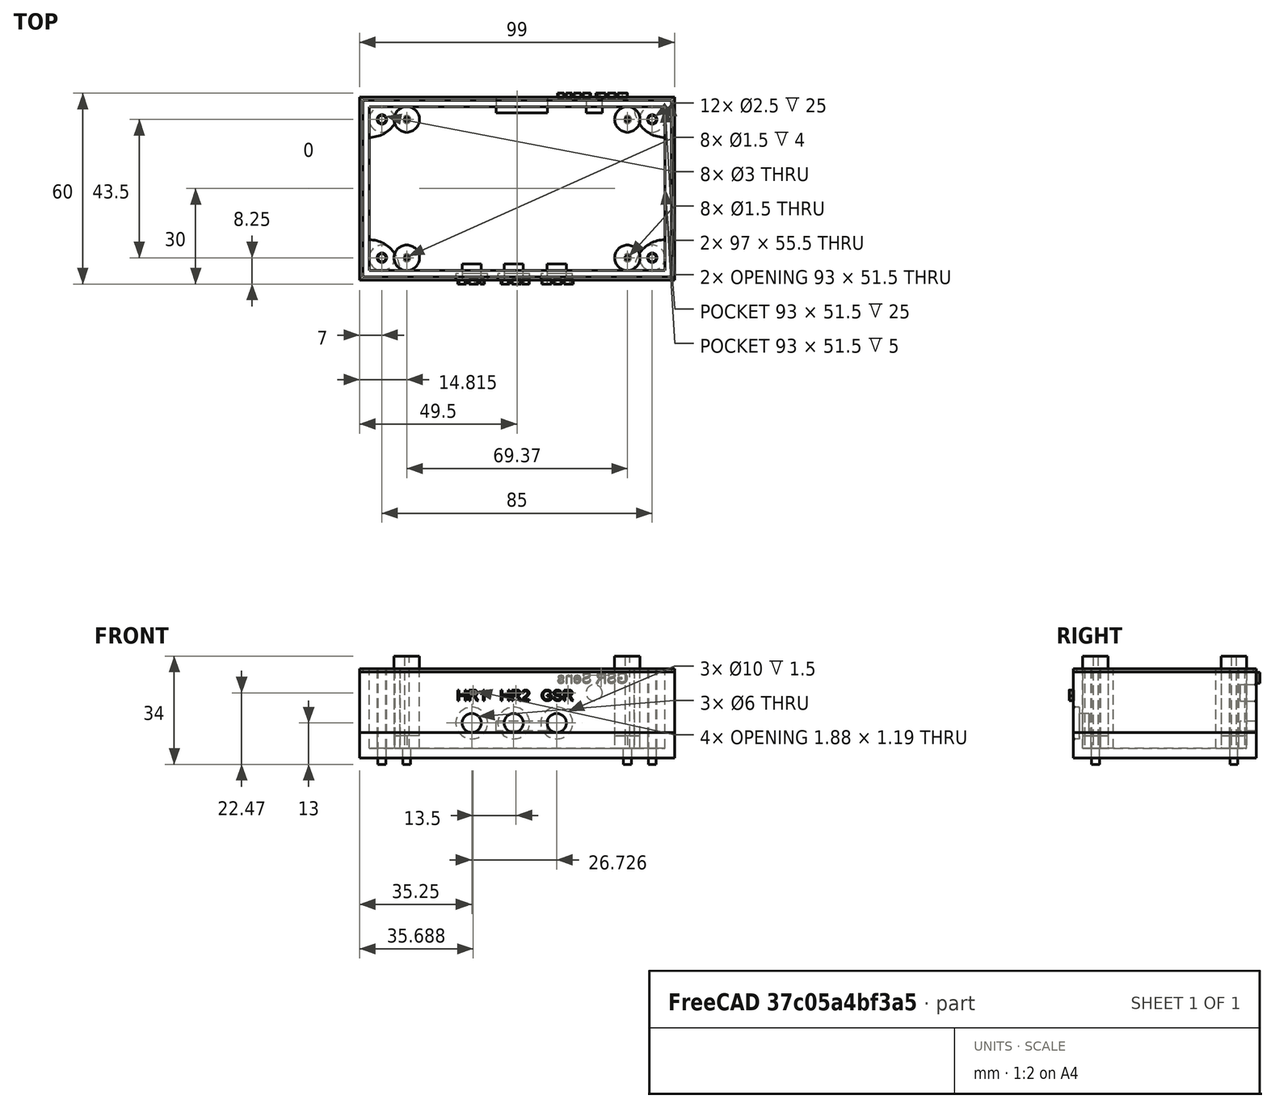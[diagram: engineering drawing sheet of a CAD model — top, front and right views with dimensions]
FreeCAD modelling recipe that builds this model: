
FCSTD DOCUMENT  (FreeCAD 0.15R4572 (Git))
Label: bottom2
License: All rights reserved
LicenseURL: http://en.wikipedia.org/wiki/All_rights_reserved
objects: Sketcher::SketchObject×22, PartDesign::Pad×13, PartDesign::Pocket×9, Part::Part2DObjectPython×4, PartDesign::Fillet×4, Part::Thickness×3, Part::Mirroring×1
note: 78 computed .brp shape members not serialized (recipe doc carries the construction recipe); baked Part::Feature solids carry a one-line shape summary decoded from their .brp

FEATURE [Sketcher::SketchObject] Sketch  label="Под отверстия платы"
  sketch-geometry (12):
    g0: LineSegment [constr] StartX=-34.685 StartY=21.75 StartZ=0 EndX=34.685 EndY=21.75 EndZ=0
    g1: LineSegment [constr] StartX=34.685 StartY=21.75 StartZ=0 EndX=34.685 EndY=-21.75 EndZ=0
    g2: LineSegment [constr] StartX=34.685 StartY=-21.75 StartZ=0 EndX=-34.685 EndY=-21.75 EndZ=0
    g3: LineSegment [constr] StartX=-34.685 StartY=-21.75 StartZ=0 EndX=-34.685 EndY=21.75 EndZ=0
    g4: Circle CenterX=-34.685 CenterY=21.75 CenterZ=0 NormalX=0 NormalY=0 NormalZ=1 Radius=0.75
    g5: Circle CenterX=-34.685 CenterY=-21.75 CenterZ=0 NormalX=0 NormalY=0 NormalZ=1 Radius=0.75
    g6: Circle CenterX=34.685 CenterY=-21.75 CenterZ=0 NormalX=0 NormalY=0 NormalZ=1 Radius=0.75
    g7: Circle CenterX=34.685 CenterY=21.75 CenterZ=0 NormalX=0 NormalY=0 NormalZ=1 Radius=0.75
    g8: Circle CenterX=-34.685 CenterY=21.75 CenterZ=0 NormalX=0 NormalY=0 NormalZ=1 Radius=4
    g9: Circle CenterX=-34.685 CenterY=-21.75 CenterZ=0 NormalX=0 NormalY=0 NormalZ=1 Radius=4
    g10: Circle CenterX=34.685 CenterY=-21.75 CenterZ=0 NormalX=0 NormalY=0 NormalZ=1 Radius=4
    g11: Circle CenterX=34.685 CenterY=21.75 CenterZ=0 NormalX=0 NormalY=0 NormalZ=1 Radius=4
  constraints (28):
    c: Coincident(g0,g1)
    c: Coincident(g1,g2)
    c: Coincident(g2,g3)
    c: Coincident(g3,g0)
    c: Horizontal(g0)
    c: Horizontal(g2)
    c: Vertical(g1)
    c: Vertical(g3)
    c: Symmetric(g0,g0,g-2)
    c: Symmetric(g0,g2,g-1)
    c: DistanceX(g0) = 69.37
    c: DistanceY(g0,g1) = -43.5
    c: Coincident(g4,g0)
    c: Coincident(g5,g2)
    c: Coincident(g6,g1)
    c: Coincident(g7,g0)
    c: Equal(g4,g7)
    c: Equal(g6,g5)
    c: Equal(g5,g4)
    c: Radius(g4) = 0.75
    c: Coincident(g8,g0)
    c: Coincident(g9,g2)
    c: Coincident(g10,g1)
    c: Coincident(g11,g0)
    c: Equal(g11,g8)
    c: Equal(g8,g9)
    c: Equal(g9,g10)
    c: Radius(g11) = 4
FEATURE [Sketcher::SketchObject] Sketch001  label="Маска платы"
  sketch-geometry (4):
    g0: LineSegment StartX=-38.25 StartY=25.25 StartZ=0 EndX=38.25 EndY=25.25 EndZ=0
    g1: LineSegment StartX=38.25 StartY=25.25 StartZ=0 EndX=38.25 EndY=-25.25 EndZ=0
    g2: LineSegment StartX=38.25 StartY=-25.25 StartZ=0 EndX=-38.25 EndY=-25.25 EndZ=0
    g3: LineSegment StartX=-38.25 StartY=-25.25 StartZ=0 EndX=-38.25 EndY=25.25 EndZ=0
  constraints (12):
    c: Coincident(g0,g1)
    c: Coincident(g1,g2)
    c: Coincident(g2,g3)
    c: Coincident(g3,g0)
    c: Horizontal(g0)
    c: Horizontal(g2)
    c: Vertical(g1)
    c: Vertical(g3)
    c: Symmetric(g0,g0,g-2)
    c: Symmetric(g0,g1,g-1)
    c: DistanceX(g0) = 76.5
    c: DistanceY(g1) = -50.5
FEATURE [Sketcher::SketchObject] Sketch002  label="Маска нижней части"
  sketch-geometry (8):
    g0: LineSegment [constr] StartX=-45 StartY=25 StartZ=0 EndX=45 EndY=25 EndZ=0
    g1: LineSegment [constr] StartX=45 StartY=25 StartZ=0 EndX=45 EndY=-25 EndZ=0
    g2: LineSegment [constr] StartX=45 StartY=-25 StartZ=0 EndX=-45 EndY=-25 EndZ=0
    g3: LineSegment [constr] StartX=-45 StartY=-25 StartZ=0 EndX=-45 EndY=25 EndZ=0
    g4: LineSegment StartX=-46.5 StartY=25.75 StartZ=0 EndX=46.5 EndY=25.75 EndZ=0
    g5: LineSegment StartX=46.5 StartY=25.75 StartZ=0 EndX=46.5 EndY=-25.75 EndZ=0
    g6: LineSegment StartX=46.5 StartY=-25.75 StartZ=0 EndX=-46.5 EndY=-25.75 EndZ=0
    g7: LineSegment StartX=-46.5 StartY=-25.75 StartZ=0 EndX=-46.5 EndY=25.75 EndZ=0
  constraints (24):
    c: Coincident(g0,g1)
    c: Coincident(g1,g2)
    c: Coincident(g2,g3)
    c: Coincident(g3,g0)
    c: Horizontal(g0)
    c: Horizontal(g2)
    c: Vertical(g1)
    c: Vertical(g3)
    c: Symmetric(g0,g0,g-2)
    c: Symmetric(g0,g1,g-1)
    c: DistanceX(g0) = 90
    c: DistanceY(g1) = -50
    c: Coincident(g4,g5)
    c: Coincident(g5,g6)
    c: Coincident(g6,g7)
    c: Coincident(g7,g4)
    c: Horizontal(g4)
    c: Horizontal(g6)
    c: Vertical(g5)
    c: Vertical(g7)
    c: Symmetric(g4,g5,g-1)
    c: Symmetric(g4,g4,g-2)
    c: DistanceY(g7) = 51.5
    c: DistanceX(g6) = -93
FEATURE [Sketcher::SketchObject] Sketch003  label="Отверстия под части корпуса"
  sketch-geometry (12):
    g0: LineSegment [constr] StartX=-42.5 StartY=21.75 StartZ=0 EndX=42.5 EndY=21.75 EndZ=0
    g1: LineSegment [constr] StartX=42.5 StartY=21.75 StartZ=0 EndX=42.5 EndY=-21.75 EndZ=0
    g2: LineSegment [constr] StartX=42.5 StartY=-21.75 StartZ=0 EndX=-42.5 EndY=-21.75 EndZ=0
    g3: LineSegment [constr] StartX=-42.5 StartY=-21.75 StartZ=0 EndX=-42.5 EndY=21.75 EndZ=0
    g4: Circle CenterX=-42.5 CenterY=21.75 CenterZ=0 NormalX=0 NormalY=0 NormalZ=1 Radius=1.5
    g5: Circle CenterX=-42.5 CenterY=21.75 CenterZ=0 NormalX=0 NormalY=0 NormalZ=1 Radius=4
    g6: Circle CenterX=-42.5 CenterY=-21.75 CenterZ=0 NormalX=0 NormalY=0 NormalZ=1 Radius=1.5
    g7: Circle CenterX=42.5 CenterY=-21.75 CenterZ=0 NormalX=0 NormalY=0 NormalZ=1 Radius=1.5
    g8: Circle CenterX=42.5 CenterY=21.75 CenterZ=0 NormalX=0 NormalY=0 NormalZ=1 Radius=1.5
    g9: Circle CenterX=-42.5 CenterY=-21.75 CenterZ=0 NormalX=0 NormalY=0 NormalZ=1 Radius=4
    g10: Circle CenterX=42.5 CenterY=-21.75 CenterZ=0 NormalX=0 NormalY=0 NormalZ=1 Radius=4
    g11: Circle CenterX=42.5 CenterY=21.75 CenterZ=0 NormalX=0 NormalY=0 NormalZ=1 Radius=4
  constraints (28):
    c: Coincident(g0,g1)
    c: Coincident(g1,g2)
    c: Coincident(g2,g3)
    c: Coincident(g3,g0)
    c: Horizontal(g0)
    c: Horizontal(g2)
    c: Vertical(g1)
    c: Vertical(g3)
    c: Symmetric(g1,g0,g-1)
    c: Symmetric(g0,g0,g-2)
    c: DistanceY(g1) = -43.5
    c: DistanceX(g0) = 85
    c: Coincident(g4,g0)
    c: Coincident(g5,g0)
    c: Coincident(g6,g2)
    c: Coincident(g7,g1)
    c: Coincident(g8,g0)
    c: Equal(g8,g7)
    c: Equal(g7,g6)
    c: Equal(g6,g4)
    c: Radius(g7) = 1.5
    c: Coincident(g9,g2)
    c: Coincident(g10,g1)
    c: Coincident(g11,g0)
    c: Equal(g11,g10)
    c: Equal(g10,g9)
    c: Equal(g9,g5)
    c: Radius(g9) = 4
FEATURE [PartDesign::Pad] Pad
  Length = 5
  Length2 = 100
  Sketch = -> Sketch002
  Type = 0
FEATURE [Part::Thickness] Thickness  label="Нижняя часть корпуса"
  Faces = -> Pad [Face6]
  Intersection = false
  Join = 2
  Mode = 0
  SelfIntersection = false
  Value = 3
FEATURE [PartDesign::Pad] Pad001  label="Под отверстия платы001"
  Length = 4
  Length2 = 100
  Sketch = -> Sketch
  Type = 0
FEATURE [PartDesign::Pad] Pad002  label="Отверстия под части корпуса001"
  Length = 5
  Length2 = 100
  Sketch = -> Sketch003
  Type = 0
FEATURE [Sketcher::SketchObject] Sketch004  label="Отверстия"
  sketch-geometry (16):
    g0: LineSegment [constr] StartX=-34.685 StartY=21.75 StartZ=0 EndX=34.685 EndY=21.75 EndZ=0
    g1: LineSegment [constr] StartX=34.685 StartY=21.75 StartZ=0 EndX=34.685 EndY=-21.75 EndZ=0
    g2: LineSegment [constr] StartX=34.685 StartY=-21.75 StartZ=0 EndX=-34.685 EndY=-21.75 EndZ=0
    g3: LineSegment [constr] StartX=-34.685 StartY=-21.75 StartZ=0 EndX=-34.685 EndY=21.75 EndZ=0
    g4: LineSegment [constr] StartX=-42.5 StartY=21.75 StartZ=0 EndX=42.5 EndY=21.75 EndZ=0
    g5: LineSegment [constr] StartX=42.5 StartY=21.75 StartZ=0 EndX=42.5 EndY=-21.75 EndZ=0
    g6: LineSegment [constr] StartX=42.5 StartY=-21.75 StartZ=0 EndX=-42.5 EndY=-21.75 EndZ=0
    g7: LineSegment [constr] StartX=-42.5 StartY=-21.75 StartZ=0 EndX=-42.5 EndY=21.75 EndZ=0
    g8: Circle CenterX=-42.5 CenterY=21.75 CenterZ=0 NormalX=0 NormalY=0 NormalZ=1 Radius=1.25
    g9: Circle CenterX=-34.685 CenterY=21.75 CenterZ=0 NormalX=0 NormalY=0 NormalZ=1 Radius=1.25
    g10: Circle CenterX=-42.5 CenterY=-21.75 CenterZ=0 NormalX=0 NormalY=0 NormalZ=1 Radius=1.25
    g11: Circle CenterX=-34.685 CenterY=-21.75 CenterZ=0 NormalX=0 NormalY=0 NormalZ=1 Radius=1.25
    g12: Circle CenterX=34.685 CenterY=-21.75 CenterZ=0 NormalX=0 NormalY=0 NormalZ=1 Radius=1.25
    g13: Circle CenterX=42.5 CenterY=-21.75 CenterZ=0 NormalX=0 NormalY=0 NormalZ=1 Radius=1.25
    g14: Circle CenterX=34.685 CenterY=21.75 CenterZ=0 NormalX=0 NormalY=0 NormalZ=1 Radius=1.25
    g15: Circle CenterX=42.5 CenterY=21.75 CenterZ=0 NormalX=0 NormalY=0 NormalZ=1 Radius=1.25
  constraints (40):
    c: Coincident(g0,g1)
    c: Coincident(g1,g2)
    c: Coincident(g2,g3)
    c: Coincident(g3,g0)
    c: Horizontal(g0)
    c: Horizontal(g2)
    c: Vertical(g1)
    c: Vertical(g3)
    c: Symmetric(g0,g0,g-2)
    c: DistanceX(g0) = 69.37
    c: Symmetric(g0,g1,g-1)
    c: DistanceY(g1) = -43.5
    c: Coincident(g4,g5)
    c: Coincident(g5,g6)
    c: Coincident(g6,g7)
    c: Coincident(g7,g4)
    c: Horizontal(g4)
    c: Horizontal(g6)
    c: Vertical(g5)
    c: Vertical(g7)
    c: Symmetric(g5,g4,g-1)
    c: Symmetric(g4,g4,g-2)
    c: DistanceY(g5) = -43.5
    c: DistanceX(g6,g5) = 85
    c: Coincident(g8,g4)
    c: Coincident(g9,g0)
    c: Coincident(g10,g6)
    c: Coincident(g11,g2)
    c: Coincident(g12,g1)
    c: Coincident(g13,g5)
    c: Coincident(g14,g0)
    c: Coincident(g15,g4)
    c: Equal(g15,g14)
    c: Equal(g14,g13)
    c: Equal(g13,g12)
    c: Equal(g12,g10)
    c: Equal(g10,g11)
    c: Equal(g11,g8)
    c: Equal(g8,g9)
    c: Radius(g8) = 1.25
FEATURE [Sketcher::SketchObject] Sketch005  label="Отверстия001"
  Support = -> Thickness [Face5]
  sketch-geometry (16):
    g0: LineSegment [constr] StartX=-34.7 StartY=21.75 StartZ=0 EndX=34.7 EndY=21.75 EndZ=0
    g1: LineSegment [constr] StartX=34.7 StartY=21.75 StartZ=0 EndX=34.7 EndY=-21.75 EndZ=0
    g2: LineSegment [constr] StartX=34.7 StartY=-21.75 StartZ=0 EndX=-34.7 EndY=-21.75 EndZ=0
    g3: LineSegment [constr] StartX=-34.7 StartY=-21.75 StartZ=0 EndX=-34.7 EndY=21.75 EndZ=0
    g4: LineSegment [constr] StartX=-42.5 StartY=21.75 StartZ=0 EndX=42.5 EndY=21.75 EndZ=0
    g5: LineSegment [constr] StartX=42.5 StartY=21.75 StartZ=0 EndX=42.5 EndY=-21.75 EndZ=0
    g6: LineSegment [constr] StartX=42.5 StartY=-21.75 StartZ=0 EndX=-42.5 EndY=-21.75 EndZ=0
    g7: LineSegment [constr] StartX=-42.5 StartY=-21.75 StartZ=0 EndX=-42.5 EndY=21.75 EndZ=0
    g8: Circle CenterX=-42.5 CenterY=21.75 CenterZ=0 NormalX=0 NormalY=0 NormalZ=1 Radius=1.25
    g9: Circle CenterX=-34.7 CenterY=21.75 CenterZ=0 NormalX=0 NormalY=0 NormalZ=1 Radius=1.25
    g10: Circle CenterX=34.7 CenterY=21.75 CenterZ=0 NormalX=0 NormalY=0 NormalZ=1 Radius=1.25
    g11: Circle CenterX=42.5 CenterY=21.75 CenterZ=0 NormalX=0 NormalY=0 NormalZ=1 Radius=1.25
    g12: Circle CenterX=42.5 CenterY=-21.75 CenterZ=0 NormalX=0 NormalY=0 NormalZ=1 Radius=1.25
    g13: Circle CenterX=34.7 CenterY=-21.75 CenterZ=0 NormalX=0 NormalY=0 NormalZ=1 Radius=1.25
    g14: Circle CenterX=-42.5 CenterY=-21.75 CenterZ=0 NormalX=0 NormalY=0 NormalZ=1 Radius=1.25
    g15: Circle CenterX=-34.7 CenterY=-21.75 CenterZ=0 NormalX=0 NormalY=0 NormalZ=1 Radius=1.25
  constraints (40):
    c: Coincident(g0,g1)
    c: Coincident(g1,g2)
    c: Coincident(g2,g3)
    c: Coincident(g3,g0)
    c: Horizontal(g0)
    c: Horizontal(g2)
    c: Vertical(g1)
    c: Vertical(g3)
    c: Coincident(g4,g5)
    c: Coincident(g5,g6)
    c: Coincident(g6,g7)
    c: Coincident(g7,g4)
    c: Horizontal(g4)
    c: Horizontal(g6)
    c: Vertical(g5)
    c: Vertical(g7)
    c: Symmetric(g5,g4,g-1)
    c: Symmetric(g4,g4,g-2)
    c: Symmetric(g0,g0,g-2)
    c: Symmetric(g0,g1,g-1)
    c: DistanceX(g0) = 69.4
    c: DistanceX(g6) = -85
    c: Equal(g5,g1)
    c: DistanceY(g7) = 43.5
    c: Coincident(g8,g4)
    c: Coincident(g9,g0)
    c: Equal(g8,g9)
    c: Radius(g8) = 1.25
    c: Coincident(g10,g0)
    c: Coincident(g11,g4)
    c: Coincident(g12,g5)
    c: Coincident(g13,g1)
    c: Coincident(g14,g6)
    c: Coincident(g15,g2)
    c: Equal(g14,g15)
    c: Equal(g15,g13)
    c: Equal(g13,g12)
    c: Equal(g12,g10)
    c: Equal(g10,g11)
    c: Equal(g9,g11)
FEATURE [PartDesign::Pocket] Pocket
  Length = 5
  Sketch = -> Sketch005
  Type = 0
FEATURE [Sketcher::SketchObject] Sketch006  label="Гайки"
  Placement = pos=(0,0,-3) rot=(1,0,0;3.14159rad)
  Support = -> Pocket [Face19]
  sketch-geometry (63):
    g0: LineSegment [constr] StartX=42.2536 StartY=21.75 StartZ=0 EndX=42.2536 EndY=-21.75 EndZ=0
    g1: LineSegment [constr] StartX=-42.2536 StartY=-21.75 StartZ=0 EndX=-42.2536 EndY=21.75 EndZ=0
    g2: Circle CenterX=-42.5 CenterY=-21.75 CenterZ=0 NormalX=0 NormalY=0 NormalZ=1 Radius=1.5
    g3: LineSegment StartX=-40.75 StartY=-24.7811 StartZ=0 EndX=-39 EndY=-21.75 EndZ=0
    g4: LineSegment StartX=-39 StartY=-21.75 StartZ=0 EndX=-40.75 EndY=-18.7189 EndZ=0
    g5: LineSegment StartX=-40.75 StartY=-18.7189 StartZ=0 EndX=-44.25 EndY=-18.7189 EndZ=0
    g6: LineSegment StartX=-44.25 StartY=-18.7189 StartZ=0 EndX=-46 EndY=-21.75 EndZ=0
    g7: LineSegment StartX=-46 StartY=-21.75 StartZ=0 EndX=-44.25 EndY=-24.7811 EndZ=0
    g8: LineSegment StartX=-44.25 StartY=-24.7811 StartZ=0 EndX=-40.75 EndY=-24.7811 EndZ=0
    g9: Circle [constr] CenterX=-42.5 CenterY=-21.75 CenterZ=0 NormalX=0 NormalY=0 NormalZ=1 Radius=3.5
    g10: LineSegment [constr] StartX=-34.7 StartY=-21.7429 StartZ=0 EndX=34.7 EndY=-21.7429 EndZ=0
    g11: LineSegment [constr] StartX=34.7 StartY=-21.7429 StartZ=0 EndX=34.7 EndY=21.7429 EndZ=0
    g12: LineSegment [constr] StartX=34.7 StartY=21.7429 StartZ=0 EndX=-34.7 EndY=21.7429 EndZ=0
    g13: LineSegment [constr] StartX=-34.7 StartY=21.7429 StartZ=0 EndX=-34.7 EndY=-21.7429 EndZ=0
    g14: LineSegment StartX=-32.95 StartY=-24.774 StartZ=0 EndX=-31.2 EndY=-21.7429 EndZ=0
    g15: LineSegment StartX=-31.2 StartY=-21.7429 StartZ=0 EndX=-32.95 EndY=-18.7118 EndZ=0
    g16: LineSegment StartX=-32.95 StartY=-18.7118 StartZ=0 EndX=-36.45 EndY=-18.7118 EndZ=0
    g17: LineSegment StartX=-36.45 StartY=-18.7118 StartZ=0 EndX=-38.2 EndY=-21.7429 EndZ=0
    g18: LineSegment StartX=-38.2 StartY=-21.7429 StartZ=0 EndX=-36.45 EndY=-24.774 EndZ=0
    g19: LineSegment StartX=-36.45 StartY=-24.774 StartZ=0 EndX=-32.95 EndY=-24.774 EndZ=0
    g20: Circle [constr] CenterX=-34.7 CenterY=-21.7429 CenterZ=0 NormalX=0 NormalY=0 NormalZ=1 Radius=3.5
    g21: LineSegment StartX=-40.75 StartY=18.7189 StartZ=0 EndX=-39 EndY=21.75 EndZ=0
    g22: LineSegment StartX=-39 StartY=21.75 StartZ=0 EndX=-40.75 EndY=24.7811 EndZ=0
    g23: LineSegment StartX=-40.75 StartY=24.7811 StartZ=0 EndX=-44.25 EndY=24.7811 EndZ=0
    g24: LineSegment StartX=-44.25 StartY=24.7811 StartZ=0 EndX=-46 EndY=21.75 EndZ=0
    g25: LineSegment StartX=-46 StartY=21.75 StartZ=0 EndX=-44.25 EndY=18.7189 EndZ=0
    g26: LineSegment StartX=-44.25 StartY=18.7189 StartZ=0 EndX=-40.75 EndY=18.7189 EndZ=0
    g27: Circle [constr] CenterX=-42.5 CenterY=21.75 CenterZ=0 NormalX=0 NormalY=0 NormalZ=1 Radius=3.5
    g28: LineSegment StartX=-32.95 StartY=18.7118 StartZ=0 EndX=-31.2 EndY=21.7429 EndZ=0
    g29: LineSegment StartX=-31.2 StartY=21.7429 StartZ=0 EndX=-32.95 EndY=24.774 EndZ=0
    g30: LineSegment StartX=-32.95 StartY=24.774 StartZ=0 EndX=-36.45 EndY=24.774 EndZ=0
    g31: LineSegment StartX=-36.45 StartY=24.774 StartZ=0 EndX=-38.2 EndY=21.7429 EndZ=0
    g32: LineSegment StartX=-38.2 StartY=21.7429 StartZ=0 EndX=-36.45 EndY=18.7118 EndZ=0
    g33: LineSegment StartX=-36.45 StartY=18.7118 StartZ=0 EndX=-32.95 EndY=18.7118 EndZ=0
    g34: Circle [constr] CenterX=-34.7 CenterY=21.7429 CenterZ=0 NormalX=0 NormalY=0 NormalZ=1 Radius=3.5
    g35: LineSegment StartX=36.45 StartY=18.7118 StartZ=0 EndX=38.2 EndY=21.7429 EndZ=0
    g36: LineSegment StartX=38.2 StartY=21.7429 StartZ=0 EndX=36.45 EndY=24.774 EndZ=0
    g37: LineSegment StartX=36.45 StartY=24.774 StartZ=0 EndX=32.95 EndY=24.774 EndZ=0
    g38: LineSegment StartX=32.95 StartY=24.774 StartZ=0 EndX=31.2 EndY=21.7429 EndZ=0
    g39: LineSegment StartX=31.2 StartY=21.7429 StartZ=0 EndX=32.95 EndY=18.7118 EndZ=0
    g40: LineSegment StartX=32.95 StartY=18.7118 StartZ=0 EndX=36.45 EndY=18.7118 EndZ=0
    g41: Circle [constr] CenterX=34.7 CenterY=21.7429 CenterZ=0 NormalX=0 NormalY=0 NormalZ=1 Radius=3.5
    g42: LineSegment StartX=44.25 StartY=18.7189 StartZ=0 EndX=46 EndY=21.75 EndZ=0
    g43: LineSegment StartX=46 StartY=21.75 StartZ=0 EndX=44.25 EndY=24.7811 EndZ=0
    g44: LineSegment StartX=44.25 StartY=24.7811 StartZ=0 EndX=40.75 EndY=24.7811 EndZ=0
    g45: LineSegment StartX=40.75 StartY=24.7811 StartZ=0 EndX=39 EndY=21.75 EndZ=0
    g46: LineSegment StartX=39 StartY=21.75 StartZ=0 EndX=40.75 EndY=18.7189 EndZ=0
    g47: LineSegment StartX=40.75 StartY=18.7189 StartZ=0 EndX=44.25 EndY=18.7189 EndZ=0
    g48: Circle [constr] CenterX=42.5 CenterY=21.75 CenterZ=0 NormalX=0 NormalY=0 NormalZ=1 Radius=3.5
    g49: LineSegment StartX=36.45 StartY=-24.774 StartZ=0 EndX=38.2 EndY=-21.7429 EndZ=0
    g50: LineSegment StartX=38.2 StartY=-21.7429 StartZ=0 EndX=36.45 EndY=-18.7118 EndZ=0
    g51: LineSegment StartX=36.45 StartY=-18.7118 StartZ=0 EndX=32.95 EndY=-18.7118 EndZ=0
    g52: LineSegment StartX=32.95 StartY=-18.7118 StartZ=0 EndX=31.2 EndY=-21.7429 EndZ=0
    g53: LineSegment StartX=31.2 StartY=-21.7429 StartZ=0 EndX=32.95 EndY=-24.774 EndZ=0
    g54: LineSegment StartX=32.95 StartY=-24.774 StartZ=0 EndX=36.45 EndY=-24.774 EndZ=0
    g55: Circle [constr] CenterX=34.7 CenterY=-21.7429 CenterZ=0 NormalX=0 NormalY=0 NormalZ=1 Radius=3.5
    g56: LineSegment StartX=44.0036 StartY=-24.7811 StartZ=0 EndX=45.7536 EndY=-21.75 EndZ=0
    g57: LineSegment StartX=45.7536 StartY=-21.75 StartZ=0 EndX=44.0036 EndY=-18.7189 EndZ=0
    g58: LineSegment StartX=44.0036 StartY=-18.7189 StartZ=0 EndX=40.5036 EndY=-18.7189 EndZ=0
    g59: LineSegment StartX=40.5036 StartY=-18.7189 StartZ=0 EndX=38.7536 EndY=-21.75 EndZ=0
    g60: LineSegment StartX=38.7536 StartY=-21.75 StartZ=0 EndX=40.5036 EndY=-24.7811 EndZ=0
    g61: LineSegment StartX=40.5036 StartY=-24.7811 StartZ=0 EndX=44.0036 EndY=-24.7811 EndZ=0
    g62: Circle [constr] CenterX=42.2536 CenterY=-21.75 CenterZ=0 NormalX=0 NormalY=0 NormalZ=1 Radius=3.5
  constraints (146):
    c: Vertical(g0)
    c: Vertical(g1)
    c: Symmetric(g0,g0,g-1)
    c: Symmetric(g0,g1,g-2)
    c: DistanceY(g0) = -43.5
    c: Radius(g2) = 1.5
    c: Coincident(g3,g4)
    c: Coincident(g4,g5)
    c: Coincident(g5,g6)
    c: Coincident(g6,g7)
    c: Coincident(g7,g8)
    c: Coincident(g8,g3)
    c: Equal(g3, g4-g8) x5
    c: PointOnObject(g3,g9)
    c: PointOnObject(g4,g9)
    c: PointOnObject(g5,g9)
    c: PointOnObject(g6,g9)
    c: PointOnObject(g7,g9)
    c: PointOnObject(g8,g9)
    c: DistanceX(g3,g6) = -7
    c: Horizontal(g5)
    c: Coincident(g10,g11)
    c: Coincident(g11,g12)
    c: Coincident(g12,g13)
    c: Coincident(g13,g10)
    c: Horizontal(g10)
    c: Horizontal(g12)
    c: Vertical(g11)
    c: Vertical(g13)
    c: Symmetric(g11,g10,g-1)
    c: Symmetric(g11,g12,g-2)
    c: DistanceX(g10,g10) = 69.4
    c: Coincident(g14,g15)
    c: Coincident(g15,g16)
    c: Coincident(g16,g17)
    c: Coincident(g17,g18)
    c: Coincident(g18,g19)
    c: Coincident(g19,g14)
    c: Equal(g14, g15-g19) x5
    c: PointOnObject(g14,g20)
    c: PointOnObject(g15,g20)
    c: PointOnObject(g16,g20)
    c: PointOnObject(g17,g20)
    c: PointOnObject(g18,g20)
    c: PointOnObject(g19,g20)
    c: Coincident(g17,g10)
    c: DistanceX(g17,g14) = 7
    c: Coincident(g20,g10)
    c: Horizontal(g16)
    c: Coincident(g21,g22)
    c: Coincident(g22,g23)
    c: Coincident(g23,g24)
    c: Coincident(g24,g25)
    c: Coincident(g25,g26)
    c: Coincident(g26,g21)
    c: Equal(g21, g22-g26) x5
    c: PointOnObject(g21,g27)
    c: PointOnObject(g22,g27)
    c: PointOnObject(g23,g27)
    c: PointOnObject(g24,g27)
    c: PointOnObject(g25,g27)
    c: PointOnObject(g26,g27)
    c: DistanceX(g24,g21) = 7
    c: Horizontal(g23)
    c: Coincident(g28,g29)
    c: Coincident(g29,g30)
    c: Coincident(g30,g31)
    c: Coincident(g31,g32)
    c: Coincident(g32,g33)
    c: Coincident(g33,g28)
    c: Equal(g28, g29-g33) x5
    c: PointOnObject(g28,g34)
    c: PointOnObject(g29,g34)
    c: PointOnObject(g30,g34)
    c: PointOnObject(g31,g34)
    c: PointOnObject(g32,g34)
    c: PointOnObject(g33,g34)
    c: Coincident(g31,g12)
    c: DistanceX(g31,g28) = 7
    c: Coincident(g12,g34)
    c: Horizontal(g30)
    c: Coincident(g35,g36)
    c: Coincident(g36,g37)
    c: Coincident(g37,g38)
    c: Coincident(g38,g39)
    c: Coincident(g39,g40)
    c: Coincident(g40,g35)
    c: Equal(g35, g36-g40) x5
    c: PointOnObject(g35,g41)
    c: PointOnObject(g36,g41)
    c: PointOnObject(g37,g41)
    c: PointOnObject(g38,g41)
    c: PointOnObject(g39,g41)
    c: PointOnObject(g40,g41)
    c: Coincident(g38,g11)
    c: DistanceX(g38,g35) = 7
    c: Horizontal(g37)
    c: Coincident(g42,g43)
    c: Coincident(g43,g44)
    c: Coincident(g44,g45)
    c: Coincident(g45,g46)
    c: Coincident(g46,g47)
    c: Coincident(g47,g42)
    c: Equal(g42, g43-g47) x5
    c: PointOnObject(g42,g48)
    c: PointOnObject(g43,g48)
    c: PointOnObject(g44,g48)
    c: PointOnObject(g45,g48)
    c: PointOnObject(g46,g48)
    c: PointOnObject(g47,g48)
    c: DistanceX(g45,g42) = 7
    c: Coincident(g41,g11)
    c: Horizontal(g44)
    c: Coincident(g49,g50)
    c: Coincident(g50,g51)
    c: Coincident(g51,g52)
    c: Coincident(g52,g53)
    c: Coincident(g53,g54)
    c: Coincident(g54,g49)
    c: Equal(g49, g50-g54) x5
    c: PointOnObject(g49,g55)
    c: PointOnObject(g50,g55)
    c: PointOnObject(g51,g55)
    c: PointOnObject(g52,g55)
    c: PointOnObject(g53,g55)
    c: PointOnObject(g54,g55)
    c: DistanceX(g52,g49) = 7
    c: Coincident(g55,g10)
    c: Horizontal(g51)
    c: Coincident(g56,g57)
    c: Coincident(g57,g58)
    c: Coincident(g58,g59)
    c: Coincident(g59,g60)
    c: Coincident(g60,g61)
    c: Coincident(g61,g56)
    c: Equal(g56, g57-g61) x5
    c: PointOnObject(g56,g62)
    c: PointOnObject(g57,g62)
    c: PointOnObject(g58,g62)
    c: PointOnObject(g59,g62)
    c: PointOnObject(g60,g62)
    c: PointOnObject(g61,g62)
    c: Coincident(g59,g0)
    c: DistanceX(g59,g56) = 7
    c: Coincident(g62,g0)
    c: Horizontal(g58)
FEATURE [Sketcher::SketchObject] Sketch007  label="Маска нижней части001"
  sketch-geometry (8):
    g0: LineSegment [constr] StartX=-45 StartY=25 StartZ=0 EndX=45 EndY=25 EndZ=0
    g1: LineSegment [constr] StartX=45 StartY=25 StartZ=0 EndX=45 EndY=-25 EndZ=0
    g2: LineSegment [constr] StartX=45 StartY=-25 StartZ=0 EndX=-45 EndY=-25 EndZ=0
    g3: LineSegment [constr] StartX=-45 StartY=-25 StartZ=0 EndX=-45 EndY=25 EndZ=0
    g4: LineSegment StartX=-46.5 StartY=25.75 StartZ=0 EndX=46.5 EndY=25.75 EndZ=0
    g5: LineSegment StartX=46.5 StartY=25.75 StartZ=0 EndX=46.5 EndY=-25.75 EndZ=0
    g6: LineSegment StartX=46.5 StartY=-25.75 StartZ=0 EndX=-46.5 EndY=-25.75 EndZ=0
    g7: LineSegment StartX=-46.5 StartY=-25.75 StartZ=0 EndX=-46.5 EndY=25.75 EndZ=0
  constraints (24):
    c: Coincident(g0,g1)
    c: Coincident(g1,g2)
    c: Coincident(g2,g3)
    c: Coincident(g3,g0)
    c: Horizontal(g0)
    c: Horizontal(g2)
    c: Vertical(g1)
    c: Vertical(g3)
    c: Symmetric(g0,g0,g-2)
    c: Symmetric(g0,g1,g-1)
    c: DistanceX(g0) = 90
    c: DistanceY(g1) = -50
    c: Coincident(g4,g5)
    c: Coincident(g5,g6)
    c: Coincident(g6,g7)
    c: Coincident(g7,g4)
    c: Horizontal(g4)
    c: Horizontal(g6)
    c: Vertical(g5)
    c: Vertical(g7)
    c: Symmetric(g4,g5,g-1)
    c: Symmetric(g4,g4,g-2)
    c: DistanceY(g7) = 51.5
    c: DistanceX(g6) = -93
FEATURE [Sketcher::SketchObject] Sketch008  label="Маска платы001"
  sketch-geometry (4):
    g0: LineSegment StartX=-38.25 StartY=25.25 StartZ=0 EndX=38.25 EndY=25.25 EndZ=0
    g1: LineSegment StartX=38.25 StartY=25.25 StartZ=0 EndX=38.25 EndY=-25.25 EndZ=0
    g2: LineSegment StartX=38.25 StartY=-25.25 StartZ=0 EndX=-38.25 EndY=-25.25 EndZ=0
    g3: LineSegment StartX=-38.25 StartY=-25.25 StartZ=0 EndX=-38.25 EndY=25.25 EndZ=0
  constraints (12):
    c: Coincident(g0,g1)
    c: Coincident(g1,g2)
    c: Coincident(g2,g3)
    c: Coincident(g3,g0)
    c: Horizontal(g0)
    c: Horizontal(g2)
    c: Vertical(g1)
    c: Vertical(g3)
    c: Symmetric(g0,g0,g-2)
    c: Symmetric(g0,g1,g-1)
    c: DistanceX(g0) = 76.5
    c: DistanceY(g1) = -50.5
FEATURE [PartDesign::Pad] Pad003  label="Параллелепипед_нач"
  Length = 25
  Length2 = 100
  Sketch = -> Sketch007
  Type = 0
FEATURE [Part::Thickness] Thickness001  label="Коробка"
  Faces = -> Pad003 [Face6]
  Intersection = false
  Join = 2
  Mode = 0
  SelfIntersection = false
  Value = 3
FEATURE [Sketcher::SketchObject] Sketch009  label="Отверстия под части корпуса002"
  sketch-geometry (12):
    g0: LineSegment [constr] StartX=-42.5 StartY=21.75 StartZ=0 EndX=42.5 EndY=21.75 EndZ=0
    g1: LineSegment [constr] StartX=42.5 StartY=21.75 StartZ=0 EndX=42.5 EndY=-21.75 EndZ=0
    g2: LineSegment [constr] StartX=42.5 StartY=-21.75 StartZ=0 EndX=-42.5 EndY=-21.75 EndZ=0
    g3: LineSegment [constr] StartX=-42.5 StartY=-21.75 StartZ=0 EndX=-42.5 EndY=21.75 EndZ=0
    g4: Circle CenterX=-42.5 CenterY=21.75 CenterZ=0 NormalX=0 NormalY=0 NormalZ=1 Radius=1.25
    g5: Circle CenterX=-42.5 CenterY=21.75 CenterZ=0 NormalX=0 NormalY=0 NormalZ=1 Radius=4
    g6: Circle CenterX=-42.5 CenterY=-21.75 CenterZ=0 NormalX=0 NormalY=0 NormalZ=1 Radius=1.25
    g7: Circle CenterX=42.5 CenterY=-21.75 CenterZ=0 NormalX=0 NormalY=0 NormalZ=1 Radius=1.25
    g8: Circle CenterX=42.5 CenterY=21.75 CenterZ=0 NormalX=0 NormalY=0 NormalZ=1 Radius=1.25
    g9: Circle CenterX=-42.5 CenterY=-21.75 CenterZ=0 NormalX=0 NormalY=0 NormalZ=1 Radius=4
    g10: Circle CenterX=42.5 CenterY=-21.75 CenterZ=0 NormalX=0 NormalY=0 NormalZ=1 Radius=4
    g11: Circle CenterX=42.5 CenterY=21.75 CenterZ=0 NormalX=0 NormalY=0 NormalZ=1 Radius=4
  constraints (28):
    c: Coincident(g0,g1)
    c: Coincident(g1,g2)
    c: Coincident(g2,g3)
    c: Coincident(g3,g0)
    c: Horizontal(g0)
    c: Horizontal(g2)
    c: Vertical(g1)
    c: Vertical(g3)
    c: Symmetric(g1,g0,g-1)
    c: Symmetric(g0,g0,g-2)
    c: DistanceY(g1) = -43.5
    c: DistanceX(g0) = 85
    c: Coincident(g4,g0)
    c: Coincident(g5,g0)
    c: Coincident(g6,g2)
    c: Coincident(g7,g1)
    c: Coincident(g8,g0)
    c: Equal(g8,g7)
    c: Equal(g7,g6)
    c: Equal(g6,g4)
    c: Radius(g7) = 1.25
    c: Coincident(g9,g2)
    c: Coincident(g10,g1)
    c: Coincident(g11,g0)
    c: Equal(g11,g10)
    c: Equal(g10,g9)
    c: Equal(g9,g5)
    c: Radius(g9) = 4
FEATURE [Sketcher::SketchObject] Sketch010  label="Под отверстия платы002"
  sketch-geometry (12):
    g0: LineSegment [constr] StartX=-34.685 StartY=21.75 StartZ=0 EndX=34.685 EndY=21.75 EndZ=0
    g1: LineSegment [constr] StartX=34.685 StartY=21.75 StartZ=0 EndX=34.685 EndY=-21.75 EndZ=0
    g2: LineSegment [constr] StartX=34.685 StartY=-21.75 StartZ=0 EndX=-34.685 EndY=-21.75 EndZ=0
    g3: LineSegment [constr] StartX=-34.685 StartY=-21.75 StartZ=0 EndX=-34.685 EndY=21.75 EndZ=0
    g4: Circle CenterX=-34.685 CenterY=21.75 CenterZ=0 NormalX=0 NormalY=0 NormalZ=1 Radius=0.75
    g5: Circle CenterX=-34.685 CenterY=-21.75 CenterZ=0 NormalX=0 NormalY=0 NormalZ=1 Radius=0.75
    g6: Circle CenterX=34.685 CenterY=-21.75 CenterZ=0 NormalX=0 NormalY=0 NormalZ=1 Radius=0.75
    g7: Circle CenterX=34.685 CenterY=21.75 CenterZ=0 NormalX=0 NormalY=0 NormalZ=1 Radius=0.75
    g8: Circle CenterX=-34.685 CenterY=21.75 CenterZ=0 NormalX=0 NormalY=0 NormalZ=1 Radius=4
    g9: Circle CenterX=-34.685 CenterY=-21.75 CenterZ=0 NormalX=0 NormalY=0 NormalZ=1 Radius=4
    g10: Circle CenterX=34.685 CenterY=-21.75 CenterZ=0 NormalX=0 NormalY=0 NormalZ=1 Radius=4
    g11: Circle CenterX=34.685 CenterY=21.75 CenterZ=0 NormalX=0 NormalY=0 NormalZ=1 Radius=4
  constraints (28):
    c: Coincident(g0,g1)
    c: Coincident(g1,g2)
    c: Coincident(g2,g3)
    c: Coincident(g3,g0)
    c: Horizontal(g0)
    c: Horizontal(g2)
    c: Vertical(g1)
    c: Vertical(g3)
    c: Symmetric(g0,g0,g-2)
    c: Symmetric(g0,g2,g-1)
    c: DistanceX(g0) = 69.37
    c: DistanceY(g0,g1) = -43.5
    c: Coincident(g4,g0)
    c: Coincident(g5,g2)
    c: Coincident(g6,g1)
    c: Coincident(g7,g0)
    c: Equal(g4,g7)
    c: Equal(g6,g5)
    c: Equal(g5,g4)
    c: Radius(g4) = 0.75
    c: Coincident(g8,g0)
    c: Coincident(g9,g2)
    c: Coincident(g10,g1)
    c: Coincident(g11,g0)
    c: Equal(g11,g8)
    c: Equal(g8,g9)
    c: Equal(g9,g10)
    c: Radius(g11) = 4
FEATURE [Sketcher::SketchObject] Sketch011  label="Маска нижней части002"
  Placement = pos=(0,0,25) rot=(0,0,1;0rad)
  Support = -> Thickness001 [Face6]
  sketch-geometry (8):
    g0: LineSegment StartX=-49.5 StartY=28.75 StartZ=0 EndX=49.5 EndY=28.75 EndZ=0
    g1: LineSegment StartX=49.5 StartY=28.75 StartZ=0 EndX=49.5 EndY=-28.75 EndZ=0
    g2: LineSegment StartX=49.5 StartY=-28.75 StartZ=0 EndX=-49.5 EndY=-28.75 EndZ=0
    g3: LineSegment StartX=-49.5 StartY=-28.75 StartZ=0 EndX=-49.5 EndY=28.75 EndZ=0
    g4: LineSegment StartX=-48.5 StartY=27.75 StartZ=0 EndX=48.5 EndY=27.75 EndZ=0
    g5: LineSegment StartX=48.5 StartY=27.75 StartZ=0 EndX=48.5 EndY=-27.75 EndZ=0
    g6: LineSegment StartX=48.5 StartY=-27.75 StartZ=0 EndX=-48.5 EndY=-27.75 EndZ=0
    g7: LineSegment StartX=-48.5 StartY=-27.75 StartZ=0 EndX=-48.5 EndY=27.75 EndZ=0
  constraints (24):
    c: Coincident(g0,g1)
    c: Coincident(g1,g2)
    c: Coincident(g2,g3)
    c: Coincident(g3,g0)
    c: Horizontal(g0)
    c: Horizontal(g2)
    c: Vertical(g1)
    c: Vertical(g3)
    c: Symmetric(g0,g0,g-2)
    c: Symmetric(g0,g1,g-1)
    c: DistanceX(g0) = 99
    c: DistanceY(g1) = -57.5
    c: Coincident(g4,g5)
    c: Coincident(g5,g6)
    c: Coincident(g6,g7)
    c: Coincident(g7,g4)
    c: Horizontal(g4)
    c: Horizontal(g6)
    c: Vertical(g5)
    c: Vertical(g7)
    c: Symmetric(g4,g5,g-1)
    c: Symmetric(g4,g4,g-2)
    c: DistanceY(g7) = 55.5
    c: DistanceX(g6) = -97
FEATURE [PartDesign::Pocket] Pocket002  label="Края коробки 1 мм"
  Length = 1
  Sketch = -> Sketch011
  Type = 0
FEATURE [Sketcher::SketchObject] Sketch012  label="Маска нижней части003"
  sketch-geometry (8):
    g0: LineSegment [constr] StartX=-45 StartY=25 StartZ=0 EndX=45 EndY=25 EndZ=0
    g1: LineSegment [constr] StartX=45 StartY=25 StartZ=0 EndX=45 EndY=-25 EndZ=0
    g2: LineSegment [constr] StartX=45 StartY=-25 StartZ=0 EndX=-45 EndY=-25 EndZ=0
    g3: LineSegment [constr] StartX=-45 StartY=-25 StartZ=0 EndX=-45 EndY=25 EndZ=0
    g4: LineSegment StartX=-46.5 StartY=25.75 StartZ=0 EndX=46.5 EndY=25.75 EndZ=0
    g5: LineSegment StartX=46.5 StartY=25.75 StartZ=0 EndX=46.5 EndY=-25.75 EndZ=0
    g6: LineSegment StartX=46.5 StartY=-25.75 StartZ=0 EndX=-46.5 EndY=-25.75 EndZ=0
    g7: LineSegment StartX=-46.5 StartY=-25.75 StartZ=0 EndX=-46.5 EndY=25.75 EndZ=0
  constraints (24):
    c: Coincident(g0,g1)
    c: Coincident(g1,g2)
    c: Coincident(g2,g3)
    c: Coincident(g3,g0)
    c: Horizontal(g0)
    c: Horizontal(g2)
    c: Vertical(g1)
    c: Vertical(g3)
    c: Symmetric(g0,g0,g-2)
    c: Symmetric(g0,g1,g-1)
    c: DistanceX(g0) = 90
    c: DistanceY(g1) = -50
    c: Coincident(g4,g5)
    c: Coincident(g5,g6)
    c: Coincident(g6,g7)
    c: Coincident(g7,g4)
    c: Horizontal(g4)
    c: Horizontal(g6)
    c: Vertical(g5)
    c: Vertical(g7)
    c: Symmetric(g4,g5,g-1)
    c: Symmetric(g4,g4,g-2)
    c: DistanceY(g7) = 51.5
    c: DistanceX(g6) = -93
FEATURE [PartDesign::Pad] Pad004  label="Параллелепипед_нач001"
  Length = 25
  Length2 = 100
  Sketch = -> Sketch012
  Type = 0
FEATURE [Part::Thickness] Thickness002  label="Коробка_Backup!!!!!!!!!!!!!!!!!!!!!!!!!!!!!!!!!!"
  Faces = -> Pad004 [Face6]
  Intersection = false
  Join = 2
  Mode = 0
  SelfIntersection = false
  Value = 3
FEATURE [Sketcher::SketchObject] Sketch013  label="Маска нижней части004"
  Placement = pos=(0,0,25) rot=(0,0,1;0rad)
  Support = -> Thickness002 [Face6]
  sketch-geometry (8):
    g0: LineSegment StartX=-49.5 StartY=28.75 StartZ=0 EndX=49.5 EndY=28.75 EndZ=0
    g1: LineSegment StartX=49.5 StartY=28.75 StartZ=0 EndX=49.5 EndY=-28.75 EndZ=0
    g2: LineSegment StartX=49.5 StartY=-28.75 StartZ=0 EndX=-49.5 EndY=-28.75 EndZ=0
    g3: LineSegment StartX=-49.5 StartY=-28.75 StartZ=0 EndX=-49.5 EndY=28.75 EndZ=0
    g4: LineSegment StartX=-48.5 StartY=27.75 StartZ=0 EndX=48.5 EndY=27.75 EndZ=0
    g5: LineSegment StartX=48.5 StartY=27.75 StartZ=0 EndX=48.5 EndY=-27.75 EndZ=0
    g6: LineSegment StartX=48.5 StartY=-27.75 StartZ=0 EndX=-48.5 EndY=-27.75 EndZ=0
    g7: LineSegment StartX=-48.5 StartY=-27.75 StartZ=0 EndX=-48.5 EndY=27.75 EndZ=0
  constraints (24):
    c: Coincident(g0,g1)
    c: Coincident(g1,g2)
    c: Coincident(g2,g3)
    c: Coincident(g3,g0)
    c: Horizontal(g0)
    c: Horizontal(g2)
    c: Vertical(g1)
    c: Vertical(g3)
    c: Symmetric(g0,g0,g-2)
    c: Symmetric(g0,g1,g-1)
    c: DistanceX(g0) = 99
    c: DistanceY(g1) = -57.5
    c: Coincident(g4,g5)
    c: Coincident(g5,g6)
    c: Coincident(g6,g7)
    c: Coincident(g7,g4)
    c: Horizontal(g4)
    c: Horizontal(g6)
    c: Vertical(g5)
    c: Vertical(g7)
    c: Symmetric(g4,g5,g-1)
    c: Symmetric(g4,g4,g-2)
    c: DistanceY(g7) = 55.5
    c: DistanceX(g6) = -97
FEATURE [PartDesign::Pocket] Pocket003  label="Края коробки 1 мм_Backup!!!!!!!!!!!!!!!!"
  Length = 1
  Sketch = -> Sketch013
  Type = 0
FEATURE [Sketcher::SketchObject] Sketch014  label="Отверстия под части корпуса003"
  ExternalGeometry = -> [Pocket002]
  Support = -> Pocket002 [Face4]
  sketch-geometry (24):
    g0: LineSegment [constr] StartX=-42.5 StartY=21.75 StartZ=0 EndX=42.5 EndY=21.75 EndZ=0
    g1: LineSegment [constr] StartX=42.5 StartY=21.75 StartZ=0 EndX=42.5 EndY=-21.75 EndZ=0
    g2: LineSegment [constr] StartX=42.5 StartY=-21.75 StartZ=0 EndX=-42.5 EndY=-21.75 EndZ=0
    g3: LineSegment [constr] StartX=-42.5 StartY=-21.75 StartZ=0 EndX=-42.5 EndY=21.75 EndZ=0
    g4: Circle CenterX=-42.5 CenterY=21.75 CenterZ=0 NormalX=0 NormalY=0 NormalZ=1 Radius=1.25
    g5: Circle [constr] CenterX=-42.5 CenterY=21.75 CenterZ=0 NormalX=0 NormalY=0 NormalZ=1 Radius=4
    g6: Circle CenterX=-42.5 CenterY=-21.75 CenterZ=0 NormalX=0 NormalY=0 NormalZ=1 Radius=1.25
    g7: Circle CenterX=42.5 CenterY=-21.75 CenterZ=0 NormalX=0 NormalY=0 NormalZ=1 Radius=1.25
    g8: Circle CenterX=42.5 CenterY=21.75 CenterZ=0 NormalX=0 NormalY=0 NormalZ=1 Radius=1.25
    g9: Circle [constr] CenterX=-42.5 CenterY=-21.75 CenterZ=0 NormalX=0 NormalY=0 NormalZ=1 Radius=4
    g10: Circle [constr] CenterX=42.5 CenterY=-21.75 CenterZ=0 NormalX=0 NormalY=0 NormalZ=1 Radius=4
    g11: Circle [constr] CenterX=42.5 CenterY=21.75 CenterZ=0 NormalX=0 NormalY=0 NormalZ=1 Radius=4
    g12: ArcOfCircle CenterX=-46.5 CenterY=25.75 CenterZ=0 NormalX=0 NormalY=0 NormalZ=1 Radius=9.65685 StartAngle=4.71239 EndAngle=6.28319
    g13: ArcOfCircle CenterX=-46.5 CenterY=-25.75 CenterZ=0 NormalX=0 NormalY=0 NormalZ=1 Radius=9.65685 StartAngle=0 EndAngle=1.5708
    g14: LineSegment StartX=-46.5 StartY=-16.0931 StartZ=0 EndX=-46.5 EndY=-25.75 EndZ=0
    g15: LineSegment StartX=-46.5 StartY=-25.75 StartZ=0 EndX=-36.8431 EndY=-25.75 EndZ=0
    g16: LineSegment StartX=-46.5 StartY=25.75 StartZ=0 EndX=-46.5 EndY=16.0931 EndZ=0
    g17: LineSegment StartX=-46.5 StartY=25.75 StartZ=0 EndX=-36.8431 EndY=25.75 EndZ=0
    g18: ArcOfCircle CenterX=46.5 CenterY=25.75 CenterZ=0 NormalX=0 NormalY=0 NormalZ=1 Radius=9.65685 StartAngle=3.14159 EndAngle=4.71239
    g19: ArcOfCircle CenterX=46.5 CenterY=-25.75 CenterZ=0 NormalX=0 NormalY=0 NormalZ=1 Radius=9.65685 StartAngle=1.5708 EndAngle=3.14159
    g20: LineSegment StartX=46.5 StartY=-16.0931 StartZ=0 EndX=46.5 EndY=-25.75 EndZ=0
    g21: LineSegment StartX=36.8431 StartY=-25.75 StartZ=0 EndX=46.5 EndY=-25.75 EndZ=0
    g22: LineSegment StartX=36.8431 StartY=25.75 StartZ=0 EndX=46.5 EndY=25.75 EndZ=0
    g23: LineSegment StartX=46.5 StartY=25.75 StartZ=0 EndX=46.5 EndY=16.0931 EndZ=0
  constraints (65):
    c: Coincident(g0,g1)
    c: Coincident(g1,g2)
    c: Coincident(g2,g3)
    c: Coincident(g3,g0)
    c: Horizontal(g2)
    c: Vertical(g1)
    c: Vertical(g3)
    c: Symmetric(g1,g0,g-1)
    c: Symmetric(g0,g0,g-2)
    c: DistanceY(g1) = -43.5
    c: DistanceX(g0) = 85
    c: Coincident(g4,g0)
    c: Coincident(g5,g0)
    c: Coincident(g6,g2)
    c: Coincident(g7,g1)
    c: Coincident(g8,g0)
    c: Equal(g8,g7)
    c: Equal(g7,g6)
    c: Equal(g6,g4)
    c: Radius(g7) = 1.25
    c: Coincident(g9,g2)
    c: Coincident(g10,g1)
    c: Coincident(g11,g0)
    c: Equal(g11,g10)
    c: Equal(g10,g9)
    c: Equal(g9,g5)
    c: Radius(g9) = 4
    c: Coincident(g12,g-4)
    c: PointOnObject(g12,g-3)
    c: PointOnObject(g12,g-4)
    c: Tangent(g5,g12)
    c: Coincident(g13,g-5)
    c: PointOnObject(g13,g-4)
    c: PointOnObject(g13,g-5)
    c: Tangent(g13,g9)
    c: Coincident(g14,g13)
    c: Coincident(g14,g13)
    c: Tangent(g14,g9)
    c: Coincident(g15,g13)
    c: Coincident(g15,g13)
    c: Tangent(g15,g9)
    c: Coincident(g16,g12)
    c: Coincident(g16,g12)
    c: Coincident(g17,g12)
    c: Coincident(g17,g12)
    c: Tangent(g17,g5)
    c: Coincident(g18,g-6)
    c: PointOnObject(g18,g-6)
    c: PointOnObject(g18,g-3)
    c: Tangent(g18,g11)
    c: Coincident(g19,g-6)
    c: PointOnObject(g19,g-5)
    c: PointOnObject(g19,g-6)
    c: Tangent(g19,g10)
    c: Coincident(g20,g19)
    c: Coincident(g20,g19)
    c: Tangent(g20,g10)
    c: Coincident(g21,g19)
    c: Coincident(g21,g19)
    c: Coincident(g22,g18)
    c: Coincident(g22,g18)
    c: Coincident(g23,g18)
    c: Coincident(g23,g18)
    c: Vertical(g23)
    c: Tangent(g23,g11)
FEATURE [PartDesign::Pad] Pad005  label="Угловые отверстия"
  Length = 25
  Length2 = 100
  Sketch = -> Sketch014
  Type = 0
FEATURE [Sketcher::SketchObject] Sketch017  label="Отверстия под части корпуса004"
  sketch-geometry (24):
    g0: LineSegment [constr] StartX=-42.5 StartY=21.75 StartZ=0 EndX=42.5 EndY=21.75 EndZ=0
    g1: LineSegment [constr] StartX=42.5 StartY=21.75 StartZ=0 EndX=42.5 EndY=-21.75 EndZ=0
    g2: LineSegment [constr] StartX=42.5 StartY=-21.75 StartZ=0 EndX=-42.5 EndY=-21.75 EndZ=0
    g3: LineSegment [constr] StartX=-42.5 StartY=-21.75 StartZ=0 EndX=-42.5 EndY=21.75 EndZ=0
    g4: Circle CenterX=-42.5 CenterY=21.75 CenterZ=0 NormalX=0 NormalY=0 NormalZ=1 Radius=1.5
    g5: Circle [constr] CenterX=-42.5 CenterY=21.75 CenterZ=0 NormalX=0 NormalY=0 NormalZ=1 Radius=4
    g6: Circle CenterX=-42.5 CenterY=-21.75 CenterZ=0 NormalX=0 NormalY=0 NormalZ=1 Radius=1.5
    g7: Circle CenterX=42.5 CenterY=-21.75 CenterZ=0 NormalX=0 NormalY=0 NormalZ=1 Radius=1.5
    g8: Circle CenterX=42.5 CenterY=21.75 CenterZ=0 NormalX=0 NormalY=0 NormalZ=1 Radius=1.5
    g9: Circle [constr] CenterX=-42.5 CenterY=-21.75 CenterZ=0 NormalX=0 NormalY=0 NormalZ=1 Radius=4
    g10: Circle [constr] CenterX=42.5 CenterY=-21.75 CenterZ=0 NormalX=0 NormalY=0 NormalZ=1 Radius=4
    g11: Circle [constr] CenterX=42.5 CenterY=21.75 CenterZ=0 NormalX=0 NormalY=0 NormalZ=1 Radius=4
    g12: ArcOfCircle CenterX=-46.5 CenterY=25.75 CenterZ=0 NormalX=0 NormalY=0 NormalZ=1 Radius=9.65685 StartAngle=4.71239 EndAngle=6.28319
    g13: ArcOfCircle CenterX=-46.5 CenterY=-25.75 CenterZ=0 NormalX=0 NormalY=0 NormalZ=1 Radius=9.65685 StartAngle=0 EndAngle=1.5708
    g14: LineSegment StartX=-46.5 StartY=-16.0931 StartZ=0 EndX=-46.5 EndY=-25.75 EndZ=0
    g15: LineSegment StartX=-46.5 StartY=-25.75 StartZ=0 EndX=-36.8431 EndY=-25.75 EndZ=0
    g16: LineSegment StartX=-46.5 StartY=25.75 StartZ=0 EndX=-46.5 EndY=16.0931 EndZ=0
    g17: LineSegment StartX=-46.5 StartY=25.75 StartZ=0 EndX=-36.8431 EndY=25.75 EndZ=0
    g18: ArcOfCircle CenterX=46.5 CenterY=25.75 CenterZ=0 NormalX=0 NormalY=0 NormalZ=1 Radius=9.65685 StartAngle=3.14159 EndAngle=4.71239
    g19: ArcOfCircle CenterX=46.5 CenterY=-25.75 CenterZ=0 NormalX=0 NormalY=0 NormalZ=1 Radius=9.65685 StartAngle=1.5708 EndAngle=3.14159
    g20: LineSegment StartX=46.5 StartY=-16.0931 StartZ=0 EndX=46.5 EndY=-25.75 EndZ=0
    g21: LineSegment StartX=36.8431 StartY=-25.75 StartZ=0 EndX=46.5 EndY=-25.75 EndZ=0
    g22: LineSegment StartX=36.8431 StartY=25.75 StartZ=0 EndX=46.5 EndY=25.75 EndZ=0
    g23: LineSegment StartX=46.5 StartY=25.75 StartZ=0 EndX=46.5 EndY=16.0931 EndZ=0
  constraints (53):
    c: Coincident(g0,g1)
    c: Coincident(g1,g2)
    c: Coincident(g2,g3)
    c: Coincident(g3,g0)
    c: Horizontal(g2)
    c: Vertical(g1)
    c: Vertical(g3)
    c: Symmetric(g1,g0,g-1)
    c: Symmetric(g0,g0,g-2)
    c: DistanceY(g1) = -43.5
    c: DistanceX(g0) = 85
    c: Coincident(g4,g0)
    c: Coincident(g5,g0)
    c: Coincident(g6,g2)
    c: Coincident(g7,g1)
    c: Coincident(g8,g0)
    c: Equal(g8,g7)
    c: Equal(g7,g6)
    c: Equal(g6,g4)
    c: Radius(g7) = 1.5
    c: Coincident(g9,g2)
    c: Coincident(g10,g1)
    c: Coincident(g11,g0)
    c: Equal(g11,g10)
    c: Equal(g10,g9)
    c: Equal(g9,g5)
    c: Radius(g9) = 4
    c: Tangent(g5,g12)
    c: Tangent(g13,g9)
    c: Coincident(g14,g13)
    c: Coincident(g14,g13)
    c: Tangent(g14,g9)
    c: Coincident(g15,g13)
    c: Coincident(g15,g13)
    c: Tangent(g15,g9)
    c: Coincident(g16,g12)
    c: Coincident(g16,g12)
    c: Coincident(g17,g12)
    c: Coincident(g17,g12)
    c: Tangent(g17,g5)
    c: Tangent(g18,g11)
    c: Tangent(g19,g10)
    c: Coincident(g20,g19)
    c: Coincident(g20,g19)
    c: Tangent(g20,g10)
    c: Coincident(g21,g19)
    c: Coincident(g21,g19)
    c: Coincident(g22,g18)
    c: Coincident(g22,g18)
    c: Coincident(g23,g18)
    c: Coincident(g23,g18)
    c: Vertical(g23)
    c: Tangent(g23,g11)
FEATURE [PartDesign::Pad] Pad007  label="Угловые отверстия_Backup!!!!!!!!!!!!!!!!"
  Length = 25
  Length2 = 100
  Sketch = -> Sketch017
  Type = 0
FEATURE [PartDesign::Pad] Pad008  label="Угловые отверстия & отверстия для платы"
  Length = 25
  Length2 = 100
  Sketch = -> Sketch014
  Type = 0
FEATURE [Sketcher::SketchObject] Sketch018  label="Под отверстия платы003"
  ExternalGeometry = -> [Pad008]
  Support = -> Pad008 [Face21]
  sketch-geometry (12):
    g0: LineSegment [constr] StartX=-34.685 StartY=21.75 StartZ=0 EndX=34.685 EndY=21.75 EndZ=0
    g1: LineSegment [constr] StartX=34.685 StartY=21.75 StartZ=0 EndX=34.685 EndY=-21.75 EndZ=0
    g2: LineSegment [constr] StartX=34.685 StartY=-21.75 StartZ=0 EndX=-34.685 EndY=-21.75 EndZ=0
    g3: LineSegment [constr] StartX=-34.685 StartY=-21.75 StartZ=0 EndX=-34.685 EndY=21.75 EndZ=0
    g4: Circle CenterX=-34.685 CenterY=21.75 CenterZ=0 NormalX=0 NormalY=0 NormalZ=1 Radius=0.75
    g5: Circle CenterX=-34.685 CenterY=-21.75 CenterZ=0 NormalX=0 NormalY=0 NormalZ=1 Radius=0.75
    g6: Circle CenterX=34.685 CenterY=-21.75 CenterZ=0 NormalX=0 NormalY=0 NormalZ=1 Radius=0.75
    g7: Circle CenterX=34.685 CenterY=21.75 CenterZ=0 NormalX=0 NormalY=0 NormalZ=1 Radius=0.75
    g8: Circle CenterX=-34.685 CenterY=21.75 CenterZ=0 NormalX=0 NormalY=0 NormalZ=1 Radius=4
    g9: Circle CenterX=-34.685 CenterY=-21.75 CenterZ=0 NormalX=0 NormalY=0 NormalZ=1 Radius=4
    g10: Circle CenterX=34.685 CenterY=-21.75 CenterZ=0 NormalX=0 NormalY=0 NormalZ=1 Radius=4
    g11: Circle CenterX=34.685 CenterY=21.75 CenterZ=0 NormalX=0 NormalY=0 NormalZ=1 Radius=4
  constraints (28):
    c: Coincident(g0,g1)
    c: Coincident(g1,g2)
    c: Coincident(g2,g3)
    c: Coincident(g3,g0)
    c: Horizontal(g0)
    c: Horizontal(g2)
    c: Vertical(g1)
    c: Vertical(g3)
    c: Symmetric(g0,g0,g-2)
    c: Symmetric(g0,g2,g-1)
    c: DistanceX(g0) = 69.37
    c: DistanceY(g0,g1) = -43.5
    c: Coincident(g4,g0)
    c: Coincident(g5,g2)
    c: Coincident(g6,g1)
    c: Coincident(g7,g0)
    c: Equal(g4,g7)
    c: Equal(g6,g5)
    c: Equal(g5,g4)
    c: Radius(g4) = 0.75
    c: Coincident(g8,g0)
    c: Coincident(g9,g2)
    c: Coincident(g10,g1)
    c: Coincident(g11,g0)
    c: Equal(g11,g8)
    c: Equal(g8,g9)
    c: Equal(g9,g10)
    c: Radius(g11) = 4
FEATURE [PartDesign::Pad] Pad009  label="Угловые отверстия & отверстия для платы001"
  Length = 4
  Length2 = 100
  Sketch = -> Sketch018
  Type = 0
FEATURE [Sketcher::SketchObject] Sketch019  label="Под отверстия платы004"
  ExternalGeometry = -> [Pad008]
  Placement = pos=(0,0,4) rot=(0,0,1;0rad)
  Support = -> Pad009 [Face48]
  sketch-geometry (12):
    g0: LineSegment [constr] StartX=-34.685 StartY=21.75 StartZ=0 EndX=34.685 EndY=21.75 EndZ=0
    g1: LineSegment [constr] StartX=34.685 StartY=21.75 StartZ=0 EndX=34.685 EndY=-21.75 EndZ=0
    g2: LineSegment [constr] StartX=34.685 StartY=-21.75 StartZ=0 EndX=-34.685 EndY=-21.75 EndZ=0
    g3: LineSegment [constr] StartX=-34.685 StartY=-21.75 StartZ=0 EndX=-34.685 EndY=21.75 EndZ=0
    g4: Circle CenterX=-34.685 CenterY=21.75 CenterZ=0 NormalX=0 NormalY=0 NormalZ=1 Radius=0.75
    g5: Circle CenterX=-34.685 CenterY=-21.75 CenterZ=0 NormalX=0 NormalY=0 NormalZ=1 Radius=0.75
    g6: Circle CenterX=34.685 CenterY=-21.75 CenterZ=0 NormalX=0 NormalY=0 NormalZ=1 Radius=0.75
    g7: Circle CenterX=34.685 CenterY=21.75 CenterZ=0 NormalX=0 NormalY=0 NormalZ=1 Radius=0.75
    g8: Circle CenterX=-34.685 CenterY=21.75 CenterZ=0 NormalX=0 NormalY=0 NormalZ=1 Radius=4
    g9: Circle CenterX=-34.685 CenterY=-21.75 CenterZ=0 NormalX=0 NormalY=0 NormalZ=1 Radius=4
    g10: Circle CenterX=34.685 CenterY=-21.75 CenterZ=0 NormalX=0 NormalY=0 NormalZ=1 Radius=4
    g11: Circle CenterX=34.685 CenterY=21.75 CenterZ=0 NormalX=0 NormalY=0 NormalZ=1 Radius=4
  constraints (28):
    c: Coincident(g0,g1)
    c: Coincident(g1,g2)
    c: Coincident(g2,g3)
    c: Coincident(g3,g0)
    c: Horizontal(g0)
    c: Horizontal(g2)
    c: Vertical(g1)
    c: Vertical(g3)
    c: Symmetric(g0,g0,g-2)
    c: Symmetric(g0,g2,g-1)
    c: DistanceX(g0) = 69.37
    c: DistanceY(g0,g1) = -43.5
    c: Coincident(g4,g0)
    c: Coincident(g5,g2)
    c: Coincident(g6,g1)
    c: Coincident(g7,g0)
    c: Equal(g4,g7)
    c: Equal(g6,g5)
    c: Equal(g5,g4)
    c: Radius(g4) = 0.75
    c: Coincident(g8,g0)
    c: Coincident(g9,g2)
    c: Coincident(g10,g1)
    c: Coincident(g11,g0)
    c: Equal(g11,g8)
    c: Equal(g8,g9)
    c: Equal(g9,g10)
    c: Radius(g11) = 4
FEATURE [PartDesign::Pocket] Pocket004  label="Вырезы в четверть-цилиндрах"
  Length = 25
  Reversed = true
  Sketch = -> Sketch019
  Type = 0
FEATURE [PartDesign::Pocket] Pocket005  label="Вырезы в четверть-цилиндрах001"
  Length = 25
  Reversed = true
  Sketch = -> Sketch019
  Type = 0
FEATURE [Sketcher::SketchObject] Sketch029  label="Jack"
  Placement = pos=(0,-28.75,0) rot=(1,0,0;1.5708rad)
  Support = -> Pocket004 [Face22]
  sketch-geometry (9):
    g0: LineSegment [constr] StartX=-1.06841 StartY=-12.2851 StartZ=0 EndX=-1.06841 EndY=25 EndZ=0
    g1: LineSegment [constr] StartX=-14.25 StartY=-12.25 StartZ=0 EndX=-14.25 EndY=25 EndZ=0
    g2: LineSegment [constr] StartX=12.4755 StartY=-12.25 StartZ=0 EndX=12.4755 EndY=25 EndZ=0
    g3: Circle CenterX=-14.25 CenterY=8 CenterZ=0 NormalX=0 NormalY=0 NormalZ=1 Radius=3
    g4: Circle CenterX=-1.06841 CenterY=8 CenterZ=0 NormalX=0 NormalY=0 NormalZ=1 Radius=3
    g5: Circle CenterX=12.4755 CenterY=8 CenterZ=0 NormalX=0 NormalY=0 NormalZ=1 Radius=3
    g6: LineSegment [constr] StartX=-14.25 StartY=8 StartZ=0 EndX=-14.25 EndY=-3 EndZ=0
    g7: LineSegment [constr] StartX=-1.06841 StartY=8 StartZ=0 EndX=-1.06841 EndY=-3 EndZ=0
    g8: LineSegment [constr] StartX=12.4755 StartY=8 StartZ=0 EndX=12.4755 EndY=-3 EndZ=0
  constraints (17):
    c: Vertical(g0)
    c: Vertical(g1)
    c: Vertical(g2)
    c: PointOnObject(g3,g1)
    c: PointOnObject(g4,g0)
    c: PointOnObject(g5,g2)
    c: Equal(g5,g4)
    c: Equal(g4,g3)
    c: Coincident(g6,g3)
    c: Vertical(g6)
    c: Coincident(g7,g4)
    c: Vertical(g7)
    c: Coincident(g8,g5)
    c: Vertical(g8)
    c: DistanceY(g6) = -11
    c: Equal(g6,g7)
    c: Equal(g7,g8)
FEATURE [PartDesign::Pocket] Pocket006  label="Вырез Jack"
  Length = 5
  Sketch = -> Sketch029
  Type = 0
FEATURE [Sketcher::SketchObject] Sketch022  label="GSR"
  ExternalGeometry = -> [Pocket003]
  Placement = pos=(0,28.75,0) rot=(0,0.707107,0.707107;3.14159rad)
  Support = -> Pocket006 [Face19]
  sketch-geometry (13):
    g0: LineSegment [constr] StartX=38.25 StartY=25.25 StartZ=0 EndX=38.25 EndY=-25.25 EndZ=0
    g1: LineSegment [constr] StartX=-38.25 StartY=-25.25 StartZ=0 EndX=-38.25 EndY=25.25 EndZ=0
    g2: LineSegment [constr] StartX=-38.25 StartY=-12.25 StartZ=0 EndX=-14.25 EndY=-12.25 EndZ=0
    g3: LineSegment [constr] StartX=38.25 StartY=-12.25 StartZ=0 EndX=12.55 EndY=-12.25 EndZ=0
    g4: LineSegment [constr] StartX=-14.25 StartY=-12.25 StartZ=0 EndX=12.55 EndY=-12.25 EndZ=0
    g5: LineSegment [constr] StartX=-14.25 StartY=-12.25 StartZ=0 EndX=-14.25 EndY=-25.25 EndZ=0
    g6: LineSegment [constr] StartX=12.55 StartY=-25.25 StartZ=0 EndX=12.55 EndY=-12.25 EndZ=0
    g7: LineSegment [constr] StartX=-14.25 StartY=-12.2851 StartZ=0 EndX=-0.9119 EndY=-12.2851 EndZ=0
    g8: LineSegment [constr] StartX=-0.9119 StartY=-12.2851 StartZ=0 EndX=-0.9119 EndY=-25.2391 EndZ=0
    g9: LineSegment [constr] StartX=13.75 StartY=-12.25 StartZ=0 EndX=13.75 EndY=24.5646 EndZ=0
    g10: LineSegment [constr] StartX=-24.25 StartY=-12.25 StartZ=0 EndX=-24.25 EndY=17.5 EndZ=0
    g11: LineSegment [constr] StartX=-24.25 StartY=-3 StartZ=0 EndX=-24.25 EndY=17.5 EndZ=0
    g12: Circle CenterX=-24.25 CenterY=17.5 CenterZ=0 NormalX=0 NormalY=0 NormalZ=1 Radius=2.55
  constraints (10):
    c: Coincident(g4,g2)
    c: Coincident(g4,g3)
    c: Coincident(g2,g5)
    c: Coincident(g6,g3)
    c: Coincident(g8,g7)
    c: Vertical(g11)
    c: DistanceY(g11) = 20.5
    c: Coincident(g11,g10)
    c: Coincident(g12,g10)
    c: Radius(g12) = 2.55
FEATURE [PartDesign::Pocket] Pocket007  label="Вырез GSR003"
  Length = 5
  Sketch = -> Sketch022
  Type = 0
FEATURE [Sketcher::SketchObject] Sketch030  label="Converter"
  ExternalGeometry = -> [Pocket004]
  Placement = pos=(0,28.75,0) rot=(0,0.707107,0.707107;3.14159rad)
  Support = -> Pocket007 [Face19]
  sketch-geometry (4):
    g0: LineSegment StartX=-9.55 StartY=5.5 StartZ=0 EndX=6.55 EndY=5.5 EndZ=0
    g1: LineSegment StartX=6.55 StartY=5.5 StartZ=0 EndX=6.55 EndY=8.5 EndZ=0
    g2: LineSegment StartX=-9.55 StartY=5.5 StartZ=0 EndX=-9.55 EndY=8.5 EndZ=0
    g3: LineSegment StartX=-9.55 StartY=8.5 StartZ=0 EndX=6.55 EndY=8.5 EndZ=0
  constraints (7):
    c: Horizontal(g0)
    c: Coincident(g1,g0)
    c: Vertical(g1)
    c: Vertical(g2)
    c: Equal(g1,g2)
    c: Coincident(g3,g2)
    c: Coincident(g3,g1)
FEATURE [PartDesign::Pocket] Pocket008  label="Вырез converter"
  Length = 5
  Sketch = -> Sketch030
  Type = 0
FEATURE [Part::Part2DObjectPython] ShapeString  # Draft 2D object (typed FeaturePython)
  FontFile = <path> Regular.Ttf
  Placement = pos=(19.5,33,15) rot=(1,0,0;1.5708rad)
  Size = 3
  String = GSR Sens
  Tracking = 0
FEATURE [Part::Part2DObjectPython] ShapeString001  # Draft 2D object (typed FeaturePython)
  FontFile = <path> Regular.Ttf
  Placement = pos=(-19,-28.5,15) rot=(1,0,0;1.5708rad)
  Size = 3
  String = HR1
  Tracking = 0
FEATURE [PartDesign::Pad] Pad010  label="HR1"
  Length = 1.5
  Length2 = 100
  Placement = pos=(-19,-28.5,15) rot=(1,0,0;1.5708rad)
  Sketch = -> ShapeString001
  Type = 0
FEATURE [Part::Part2DObjectPython] ShapeString002  # Draft 2D object (typed FeaturePython)
  FontFile = <path> Regular.Ttf
  Placement = pos=(-5.5,-28.5,15) rot=(1,0,0;1.5708rad)
  Size = 3
  String = HR2
  Tracking = 0
FEATURE [Part::Part2DObjectPython] ShapeString003  # Draft 2D object (typed FeaturePython)
  FontFile = <path> Regular.Ttf
  Placement = pos=(7.5,-28.5,15) rot=(1,0,0;1.5708rad)
  Size = 3
  String = GSR
  Tracking = 0
FEATURE [PartDesign::Pad] Pad011  label="GSR001"
  Length = 1.5
  Length2 = 100
  Placement = pos=(19.5,33,15) rot=(1,0,0;1.5708rad)
  Sketch = -> ShapeString
  Type = 0
FEATURE [Part::Mirroring] Part__Mirroring  label="GSR001 (Mirror #1)"
  Base = (0,0,0)
  Normal = (1,0,0)
  Placement = pos=(54.5,-3,5.5) rot=(0,0,1;0rad)
  Source = -> Pad011
FEATURE [PartDesign::Pad] Pad012  label="GSR002"
  Length = 1.5
  Length2 = 100
  Placement = pos=(7.5,-28.5,15) rot=(1,0,0;1.5708rad)
  Sketch = -> ShapeString003
  Type = 0
FEATURE [PartDesign::Pad] Pad013  label="HR2"
  Length = 1.5
  Length2 = 100
  Placement = pos=(-5.5,-28.5,15) rot=(1,0,0;1.5708rad)
  Sketch = -> ShapeString002
  Type = 0
FEATURE [Sketcher::SketchObject] Sketch031  label="Jack001"
  Placement = pos=(0,-28.75,0) rot=(1,0,0;1.5708rad)
  Support = -> Pocket008 [Face22]
  sketch-geometry (9):
    g0: LineSegment [constr] StartX=-1.06841 StartY=-12.2851 StartZ=0 EndX=-1.06841 EndY=25 EndZ=0
    g1: LineSegment [constr] StartX=-14.25 StartY=-12.25 StartZ=0 EndX=-14.25 EndY=25 EndZ=0
    g2: LineSegment [constr] StartX=12.4755 StartY=-12.25 StartZ=0 EndX=12.4755 EndY=25 EndZ=0
    g3: Circle CenterX=-14.25 CenterY=8 CenterZ=0 NormalX=0 NormalY=0 NormalZ=1 Radius=5
    g4: Circle CenterX=-1.06841 CenterY=8 CenterZ=0 NormalX=0 NormalY=0 NormalZ=1 Radius=5
    g5: Circle CenterX=12.4755 CenterY=8 CenterZ=0 NormalX=0 NormalY=0 NormalZ=1 Radius=5
    g6: LineSegment [constr] StartX=-14.25 StartY=8 StartZ=0 EndX=-14.25 EndY=-3 EndZ=0
    g7: LineSegment [constr] StartX=-1.06841 StartY=8 StartZ=0 EndX=-1.06841 EndY=-3 EndZ=0
    g8: LineSegment [constr] StartX=12.4755 StartY=8 StartZ=0 EndX=12.4755 EndY=-3 EndZ=0
  constraints (18):
    c: Vertical(g0)
    c: Vertical(g1)
    c: Vertical(g2)
    c: PointOnObject(g3,g1)
    c: PointOnObject(g4,g0)
    c: PointOnObject(g5,g2)
    c: Equal(g5,g4)
    c: Equal(g4,g3)
    c: Coincident(g6,g3)
    c: Vertical(g6)
    c: Coincident(g7,g4)
    c: Vertical(g7)
    c: Coincident(g8,g5)
    c: Vertical(g8)
    c: DistanceY(g6) = -11
    c: Equal(g6,g7)
    c: Equal(g7,g8)
    c: Radius(g3) = 5
FEATURE [PartDesign::Pocket] Pocket009
  Length = 2
  Sketch = -> Sketch031
  Type = 0
FEATURE [PartDesign::Fillet] Fillet
  Base = -> Pocket009 [Edge97,Edge98,Edge96]
  Radius = 0.5
FEATURE [PartDesign::Fillet] Fillet001
  Base = -> Fillet [Edge28]
  Radius = 0.5
FEATURE [PartDesign::Fillet] Fillet002
  Base = -> Fillet001 [Edge29,Edge32,Edge9,Edge8]
  Radius = 2
FEATURE [PartDesign::Fillet] Fillet003
  Base = -> Fillet002 [Edge11]
  Radius = 0.5
note: 4 file-system paths scrubbed to <path> (originals preserved in the JSON sidecar)
